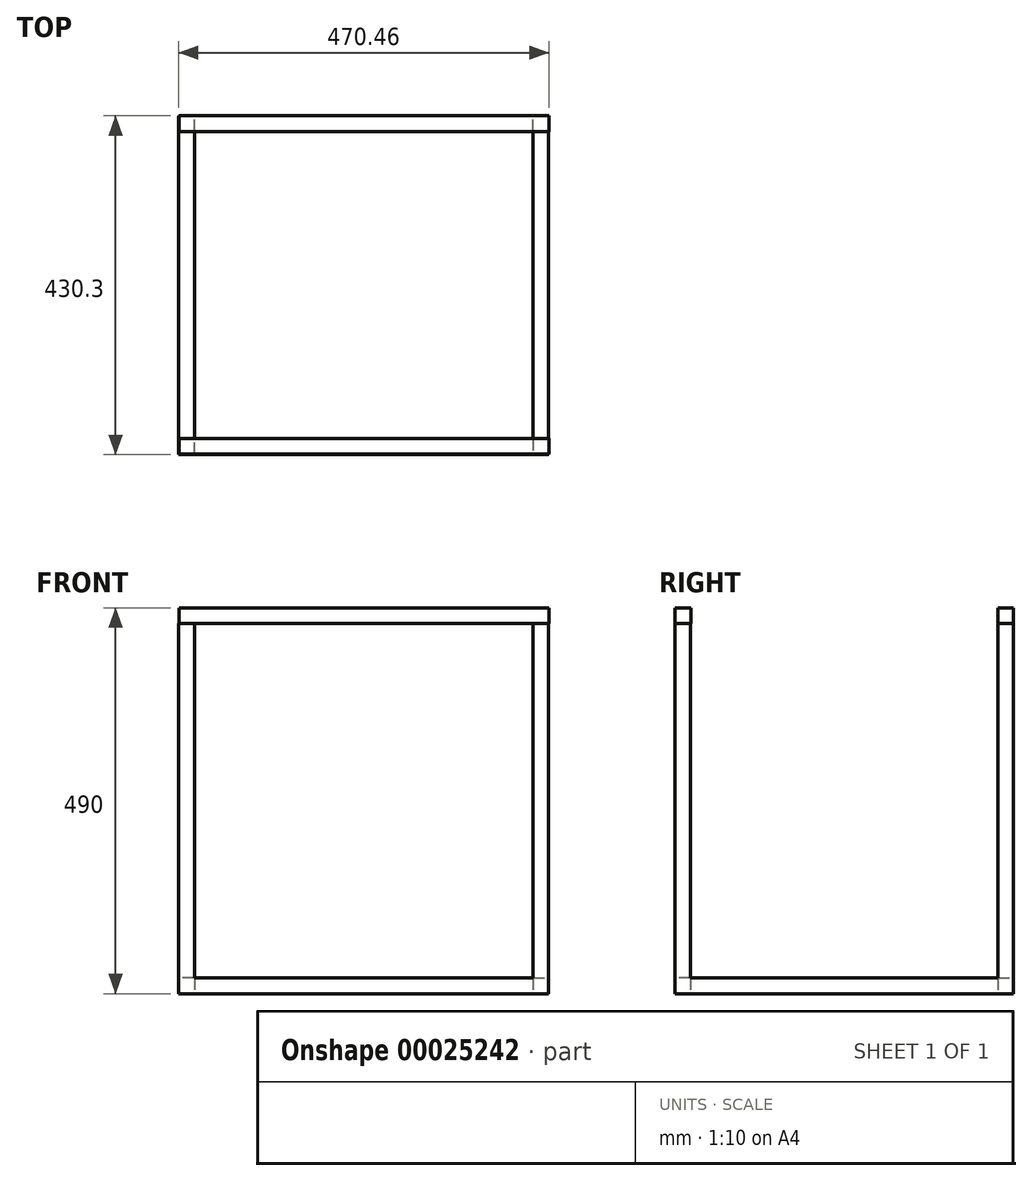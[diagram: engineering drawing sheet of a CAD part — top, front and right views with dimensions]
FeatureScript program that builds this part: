
annotation { "Feature Type Name" : "Feature", "Feature Type Description" : "" }
export const myFeature = defineFeature(function(context is Context, id is Id, definition is map)
    precondition{}
    {
        {
            var Q0;
            Q0=qCreatedBy(makeId("Top.planeOp"),FACE);
            var sketch = newSketch(context, id + "F0", { "sketchPlane" : qUnion([Q0])});
            skLineSegment(sketch, "E0.rect.bottom", {"start": v(235, 10) * mm, "end": v(-235, 10) * mm});
            skLineSegment(sketch, "E0.rect.top", {"start": v(235, -10) * mm, "end": v(-235, -10) * mm});
            skLineSegment(sketch, "E0.rect.left", {"start": v(235, 10) * mm, "end": v(235, -10) * mm});
            skLineSegment(sketch, "E0.rect.right", {"start": v(-235, 10) * mm, "end": v(-235, -10) * mm});
            skPoint(sketch, "E0.rect.middle", {"position": v(0, 0) * mm});
            skLineSegment(sketch, "E1.bottom", {"start": v(-235, 10) * mm, "end": v(-215, 10) * mm});
            skLineSegment(sketch, "E1.top", {"start": v(-235, 400) * mm, "end": v(-215, 400) * mm});
            skLineSegment(sketch, "E1.left", {"start": v(-235, 10) * mm, "end": v(-235, 400) * mm});
            skLineSegment(sketch, "E1.right", {"start": v(-215, 10) * mm, "end": v(-215, 400) * mm});
            skLineSegment(sketch, "E2.bottom", {"start": v(235, 10) * mm, "end": v(215, 10) * mm});
            skLineSegment(sketch, "E2.top", {"start": v(235, 400) * mm, "end": v(215, 400) * mm});
            skLineSegment(sketch, "E2.left", {"start": v(235, 10) * mm, "end": v(235, 400) * mm});
            skLineSegment(sketch, "E2.right", {"start": v(215, 10) * mm, "end": v(215, 400) * mm});
            skLineSegment(sketch, "E3.bottom", {"start": v(235, 400) * mm, "end": v(-235.06, 400) * mm});
            skLineSegment(sketch, "E3.top", {"start": v(235, 420) * mm, "end": v(-235.06, 420) * mm});
            skLineSegment(sketch, "E3.left", {"start": v(235, 400) * mm, "end": v(235, 420) * mm});
            skLineSegment(sketch, "E3.right", {"start": v(-235.06, 400) * mm, "end": v(-235.06, 420) * mm});
            skSolve(sketch);
        }
        {
            var Q0;
            Q0 = qSketchRegion(id + "F0", true);
            extrude(context, id + "F1", {"entities" : qUnion([Q0]), "depth" : 20 * mm});
        }
        {
            var Q0;
            Q0=makeQuery(id+"F1.opExtrude","CAP_FACE",FACE,{"disambiguationData":[OSD([sQuery(id+"F0.wireOp",EDGE,"E0.rect.bottom"),sQuery(id+"F0.wireOp",EDGE,"E0.rect.top"),sQuery(id+"F0.wireOp",EDGE,"E0.rect.left"),sQuery(id+"F0.wireOp",EDGE,"E0.rect.right"),sQuery(id+"F0.wireOp",EDGE,"E1.left"),sQuery(id+"F0.wireOp",EDGE,"E1.right"),sQuery(id+"F0.wireOp",EDGE,"E2.left"),sQuery(id+"F0.wireOp",EDGE,"E2.right"),sQuery(id+"F0.wireOp",EDGE,"E3.bottom"),sQuery(id+"F0.wireOp",EDGE,"E3.top"),sQuery(id+"F0.wireOp",EDGE,"E3.left"),sQuery(id+"F0.wireOp",EDGE,"E3.right")])],"isStart":false});
            var sketch = newSketch(context, id + "F2", { "sketchPlane" : qUnion([Q0])});
            skLineSegment(sketch, "E4.bottom", {"start": v(-235, -10) * mm, "end": v(-215, -10) * mm});
            skLineSegment(sketch, "E4.top", {"start": v(-235, 10) * mm, "end": v(-215, 10) * mm});
            skLineSegment(sketch, "E4.left", {"start": v(-235, -10) * mm, "end": v(-235, 10) * mm});
            skLineSegment(sketch, "E4.right", {"start": v(-215, -10) * mm, "end": v(-215, 10) * mm});
            skLineSegment(sketch, "E5.bottom", {"start": v(215, 10) * mm, "end": v(235, 10) * mm});
            skLineSegment(sketch, "E5.top", {"start": v(215, -10) * mm, "end": v(235, -10) * mm});
            skLineSegment(sketch, "E5.left", {"start": v(215, 10) * mm, "end": v(215, -10) * mm});
            skLineSegment(sketch, "E5.right", {"start": v(235, 10) * mm, "end": v(235, -10) * mm});
            skLineSegment(sketch, "E6.bottom", {"start": v(-215, 400) * mm, "end": v(-235.06, 400) * mm});
            skLineSegment(sketch, "E6.top", {"start": v(-215, 420) * mm, "end": v(-235.06, 420) * mm});
            skLineSegment(sketch, "E6.left", {"start": v(-215, 400) * mm, "end": v(-215, 420) * mm});
            skLineSegment(sketch, "E6.right", {"start": v(-235.06, 400) * mm, "end": v(-235.06, 420) * mm});
            skLineSegment(sketch, "E7.bottom", {"start": v(215, 400) * mm, "end": v(235, 400) * mm});
            skLineSegment(sketch, "E7.top", {"start": v(215, 420) * mm, "end": v(235, 420) * mm});
            skLineSegment(sketch, "E7.left", {"start": v(215, 400) * mm, "end": v(215, 420) * mm});
            skLineSegment(sketch, "E7.right", {"start": v(235, 400) * mm, "end": v(235, 420) * mm});
            skSolve(sketch);
        }
        {
            var Q0;
            Q0 = qSketchRegion(id + "F2", true);
            extrude(context, id + "F3", {"entities" : qUnion([Q0]), "operationType" : NewBodyOperationType.ADD, "depth" : 450 * mm});
        }
        {
            var Q0;
            Q0=makeQuery(id+"F3.opExtrude","CAP_FACE",FACE,{"disambiguationData":[OSD([sQuery(id+"F2.wireOp",EDGE,"E4.bottom"),sQuery(id+"F2.wireOp",EDGE,"E4.top"),sQuery(id+"F2.wireOp",EDGE,"E4.left"),sQuery(id+"F2.wireOp",EDGE,"E4.right")])],"isStart":false});
            var sketch = newSketch(context, id + "F4", { "sketchPlane" : qUnion([Q0])});
            skLineSegment(sketch, "E8.rect.bottom", {"start": v(235.4, 10.3) * mm, "end": v(-234.6, 10.3) * mm});
            skLineSegment(sketch, "E8.rect.top", {"start": v(235.4, -9.7) * mm, "end": v(-234.6, -9.7) * mm});
            skLineSegment(sketch, "E8.rect.left", {"start": v(235.4, 10.3) * mm, "end": v(235.4, -9.7) * mm});
            skLineSegment(sketch, "E8.rect.right", {"start": v(-234.6, 10.3) * mm, "end": v(-234.6, -9.7) * mm});
            skPoint(sketch, "E8.rect.middle", {"position": v(0.4, 0.3) * mm});
            skLineSegment(sketch, "E9.bottom", {"start": v(-234.6, 10.3) * mm, "end": v(-214.6, 10.3) * mm});
            skLineSegment(sketch, "E9.top", {"start": v(-234.6, 400.3) * mm, "end": v(-214.6, 400.3) * mm});
            skLineSegment(sketch, "E9.left", {"start": v(-234.6, 10.3) * mm, "end": v(-234.6, 400.3) * mm});
            skLineSegment(sketch, "E9.right", {"start": v(-214.6, 10.3) * mm, "end": v(-214.6, 400.3) * mm});
            skLineSegment(sketch, "E10.bottom", {"start": v(235.4, 10.3) * mm, "end": v(215.4, 10.3) * mm});
            skLineSegment(sketch, "E10.top", {"start": v(235.4, 400.3) * mm, "end": v(215.4, 400.3) * mm});
            skLineSegment(sketch, "E10.left", {"start": v(235.4, 10.3) * mm, "end": v(235.4, 400.3) * mm});
            skLineSegment(sketch, "E10.right", {"start": v(215.4, 10.3) * mm, "end": v(215.4, 400.3) * mm});
            skLineSegment(sketch, "E11.bottom", {"start": v(235.4, 400.3) * mm, "end": v(-234.67, 400.3) * mm});
            skLineSegment(sketch, "E11.top", {"start": v(235.4, 420.3) * mm, "end": v(-234.67, 420.3) * mm});
            skLineSegment(sketch, "E11.left", {"start": v(235.4, 400.3) * mm, "end": v(235.4, 420.3) * mm});
            skLineSegment(sketch, "E11.right", {"start": v(-234.67, 400.3) * mm, "end": v(-234.67, 420.3) * mm});
            skSolve(sketch);
        }
        {
            var Q0;
            Q0=makeQuery(id+"F4.imprint","IMPRINT",FACE,{"disambiguationData":[TD([[makeQuery(id+"F4.imprint","IMPRINT",EDGE,{"derivedFrom":sQuery(id+"F4.wireOp",EDGE,"E8.rect.bottom")}),1.0]])]});
            var Q1;
            Q1=makeQuery(id+"F4.imprint","IMPRINT",FACE,{"disambiguationData":[TD([[makeQuery(id+"F4.imprint","IMPRINT",EDGE,{"derivedFrom":sQuery(id+"F4.wireOp",EDGE,"E10.bottom")}),-1.0]])]});
            var Q2;
            Q2=makeQuery(id+"F4.imprint","IMPRINT",FACE,{"disambiguationData":[TD([[makeQuery(id+"F4.imprint","IMPRINT",EDGE,{"derivedFrom":sQuery(id+"F4.wireOp",EDGE,"E11.top")}),1.0]])]});
            var Q3;
            Q3=makeQuery(id+"F4.imprint","IMPRINT",FACE,{"disambiguationData":[TD([[makeQuery(id+"F4.imprint","IMPRINT",EDGE,{"derivedFrom":sQuery(id+"F4.wireOp",EDGE,"E9.bottom")}),1.0]])]});
            var Q4;
            {var subQ1=sQuery(id+"F4.wireOp",EDGE,"E8.rect.top");var subQ5=sQuery(id+"F4.wireOp",EDGE,"E8.rect.right");var subQ7=makeQuery(id+"F4.imprint","INTERSECT",VERTEX,{"derivedFrom":[subQ1,subQ5]});Q4=makeQuery(id+"F4.imprint","IMPRINT",FACE,{"disambiguationData":[TD([[makeQuery(id+"F4.imprint","IMPRINT",EDGE,{"disambiguationData":[TD([[subQ7,1.0]])],"derivedFrom":subQ1}),-1.0]])]});}
            extrude(context, id + "F5", {"entities" : qUnion([Q0, Q1, Q2, Q3, Q4]), "operationType" : NewBodyOperationType.ADD, "depth" : 20 * mm});
        }
    });
